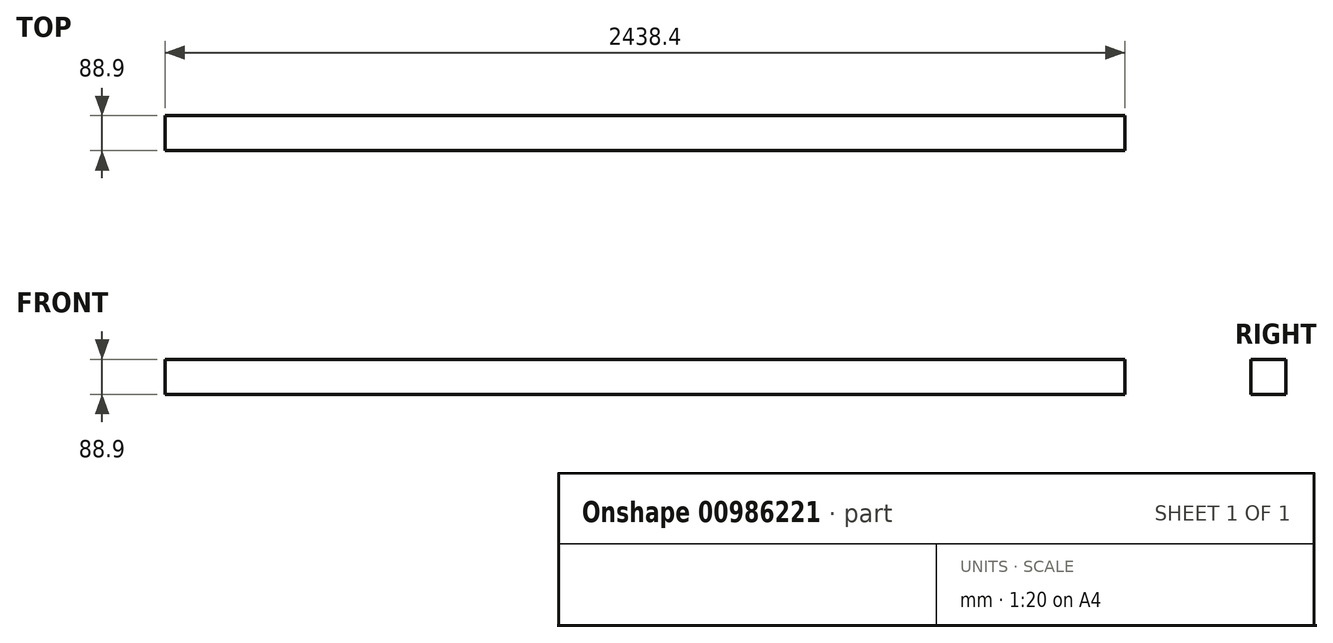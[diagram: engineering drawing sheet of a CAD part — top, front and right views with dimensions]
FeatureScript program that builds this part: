
annotation { "Feature Type Name" : "Feature", "Feature Type Description" : "" }
export const myFeature = defineFeature(function(context is Context, id is Id, definition is map)
    precondition{}
    {
        {
            var Q0;
            Q0=qCreatedBy(makeId("Right.planeOp"),FACE);
            var sketch = newSketch(context, id + "F0", { "sketchPlane" : qUnion([Q0])});
            skLineSegment(sketch, "E0.bottom", {"start": v(-44.45, 44.45) * mm, "end": v(44.45, 44.45) * mm});
            skLineSegment(sketch, "E0.top", {"start": v(-44.45, -44.45) * mm, "end": v(44.45, -44.45) * mm});
            skLineSegment(sketch, "E0.left", {"start": v(-44.45, 44.45) * mm, "end": v(-44.45, -44.45) * mm});
            skLineSegment(sketch, "E0.right", {"start": v(44.45, 44.45) * mm, "end": v(44.45, -44.45) * mm});
            skPoint(sketch, "E0.middle", {"position": v(0, 0) * mm});
            skSolve(sketch);
        }
        {
            var Q0;
            Q0=makeQuery(id+"F0.imprint","IMPRINT",FACE,{"disambiguationData":[TD([[makeQuery(id+"F0.imprint","IMPRINT",EDGE,{"derivedFrom":sQuery(id+"F0.wireOp",EDGE,"E0.bottom")}),-1.0]])]});
            extrude(context, id + "F1", {"entities" : qUnion([Q0]), "depth" : 2438.4 * mm, "offsetDistance" : 25.4 * mm});
        }
    });
